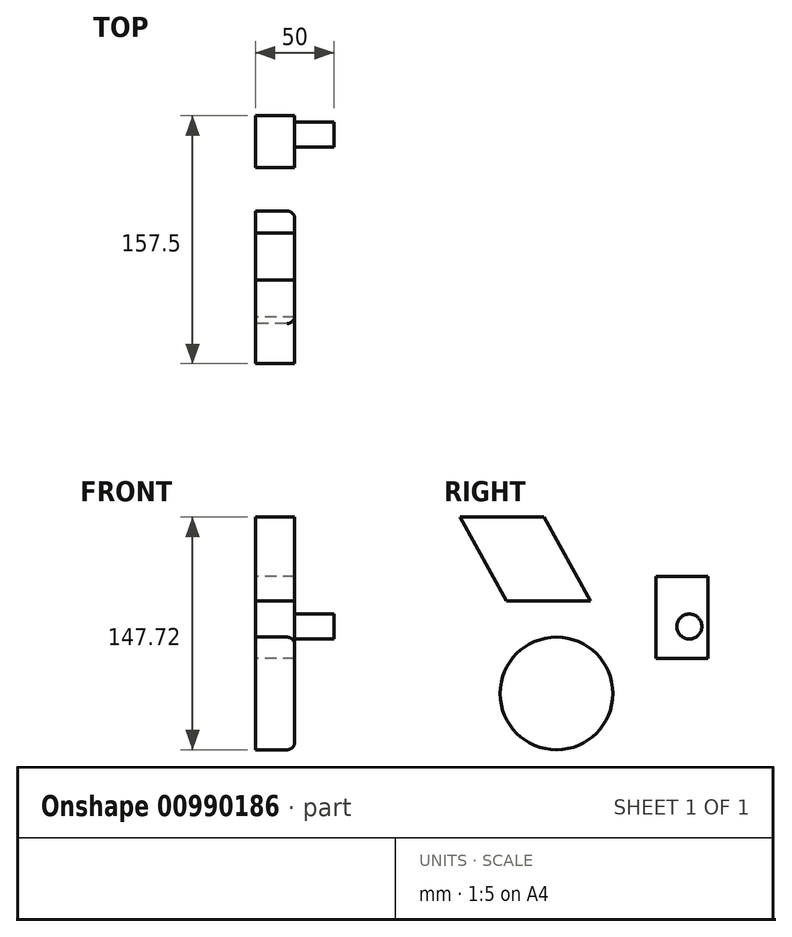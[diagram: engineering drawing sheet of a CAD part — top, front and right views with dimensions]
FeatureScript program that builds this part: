
annotation { "Feature Type Name" : "Feature", "Feature Type Description" : "" }
export const myFeature = defineFeature(function(context is Context, id is Id, definition is map)
    precondition{}
    {
        {
            var Q0;
            Q0=qCreatedBy(makeId("Right.planeOp"),FACE);
            var sketch = newSketch(context, id + "F0", { "sketchPlane" : qUnion([Q0])});
            skLineSegment(sketch, "E0", {"start": v(-57.76, 65.58) * mm, "end": v(-28.15, 12.43) * mm});
            skLineSegment(sketch, "E1", {"start": v(-28.15, 12.43) * mm, "end": v(25.1, 12.43) * mm});
            skLineSegment(sketch, "E2", {"start": v(25.1, 12.43) * mm, "end": v(-4.51, 65.58) * mm});
            skLineSegment(sketch, "E3", {"start": v(-4.51, 65.58) * mm, "end": v(-57.76, 65.58) * mm});
            skCircle(sketch, "E4", {"center": v(3.49, -46.38) * mm, "radius": 35.77 * mm});
            skPoint(sketch, "E4.first.point", {"position": v(0, -10.78) * mm});
            skPoint(sketch, "E4.second.point", {"position": v(35.46, -30.35) * mm});
            skPoint(sketch, "E4.third.point", {"position": v(-28.02, -29.45) * mm});
            skLineSegment(sketch, "E5", {"start": v(90.84, 73.34) * mm, "end": v(80.35, 30.7) * mm});
            skLineSegment(sketch, "E6.bottom", {"start": v(99.74, 28.04) * mm, "end": v(66.8, 28.04) * mm});
            skLineSegment(sketch, "E6.top", {"start": v(99.74, -24.08) * mm, "end": v(66.8, -24.08) * mm});
            skLineSegment(sketch, "E6.left", {"start": v(99.74, 28.04) * mm, "end": v(99.74, -24.08) * mm});
            skLineSegment(sketch, "E6.right", {"start": v(66.8, 28.04) * mm, "end": v(66.8, -24.08) * mm});
            skSolve(sketch);
        }
        {
            var Q0;
            Q0 = qSketchRegion(id + "F0", true);
            extrude(context, id + "F1", {"entities" : qUnion([Q0]), "depth" : 25 * mm, "offsetDistance" : 25 * mm});
        }
        {
            var Q0;
            Q0=makeQuery(id+"F1.opExtrude","CAP_EDGE",EDGE,{"disambiguationData":[OSD([sQuery(id+"F0.wireOp",EDGE,"E4")])],"isStart":false});
            fillet(context, id + "F2", {"entities" : qUnion([Q0]), "radius" : 5 * mm, "tangentPropagation" : true, "allowEdgeOverflow" : false});
        }
        {
            var Q0;
            Q0=makeQuery(id+"F1.opExtrude","CAP_FACE",FACE,{"disambiguationData":[OSD([sQuery(id+"F0.wireOp",EDGE,"E6.bottom"),sQuery(id+"F0.wireOp",EDGE,"E6.top"),sQuery(id+"F0.wireOp",EDGE,"E6.left"),sQuery(id+"F0.wireOp",EDGE,"E6.right")])],"isStart":false});
            var sketch = newSketch(context, id + "F3", { "sketchPlane" : qUnion([Q0])});
            skCircle(sketch, "E7", {"center": v(87.84, -3.87) * mm, "radius": 7.93 * mm});
            skSolve(sketch);
        }
        {
            var Q0;
            Q0 = qSketchRegion(id + "F3", true);
            extrude(context, id + "F4", {"entities" : qUnion([Q0]), "operationType" : NewBodyOperationType.ADD, "depth" : 25 * mm, "offsetDistance" : 25 * mm});
        }
    });
